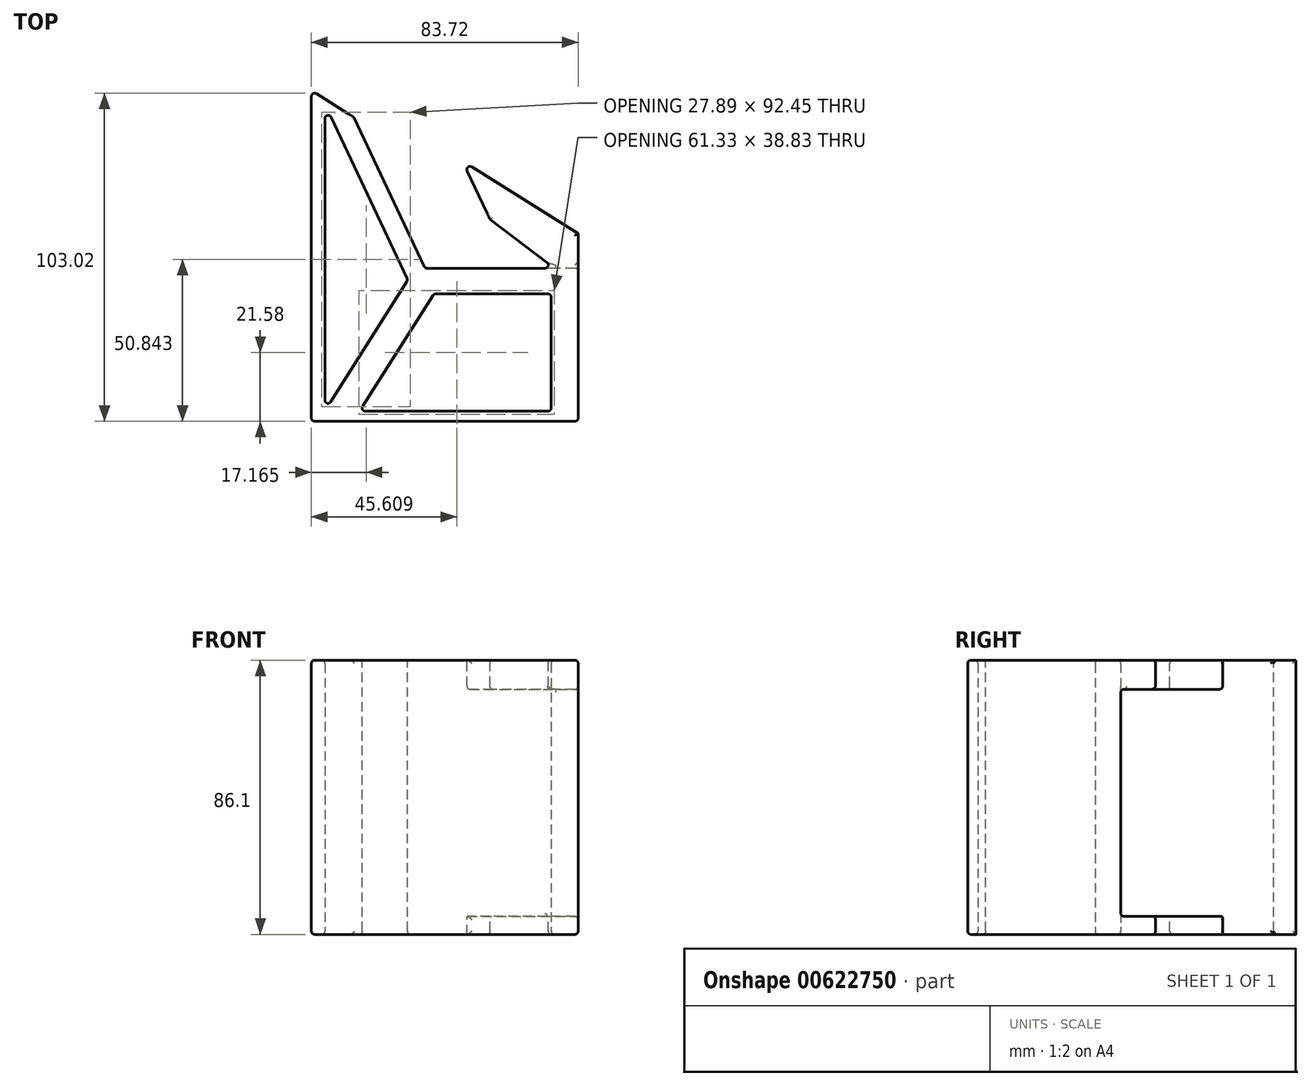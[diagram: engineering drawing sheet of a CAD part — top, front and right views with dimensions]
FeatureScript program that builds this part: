
annotation { "Feature Type Name" : "Feature", "Feature Type Description" : "" }
export const myFeature = defineFeature(function(context is Context, id is Id, definition is map)
    precondition{}
    {
        {
            var Q0;
            Q0=qCreatedBy(makeId("Top.planeOp"),FACE);
            var sketch = newSketch(context, id + "F0", { "sketchPlane" : qUnion([Q0])});
            skLineSegment(sketch, "E0", {"start": v(-40.98, 52.59) * mm, "end": v(-40.98, -58.92) * mm});
            skLineSegment(sketch, "E1", {"start": v(-40.98, -58.92) * mm, "end": v(42.74, -58.92) * mm});
            skLineSegment(sketch, "E2", {"start": v(42.74, -58.92) * mm, "end": v(42.74, 0) * mm});
            skLineSegment(sketch, "E3", {"start": v(42.74, 0) * mm, "end": v(-40.98, 52.59) * mm});
            skLineSegment(sketch, "E4", {"start": v(-36.76, 40.63) * mm, "end": v(-36.76, -55.75) * mm});
            skLineSegment(sketch, "E5", {"start": v(-36.76, -55.75) * mm, "end": v(-10.73, -14.6) * mm});
            skLineSegment(sketch, "E6", {"start": v(-10.73, -14.6) * mm, "end": v(-36.76, 40.63) * mm});
            skLineSegment(sketch, "E7", {"start": v(-25.85, -55.75) * mm, "end": v(-2.56, -18.93) * mm});
            skLineSegment(sketch, "E8", {"start": v(-2.56, -18.93) * mm, "end": v(34.3, -18.93) * mm});
            skLineSegment(sketch, "E9", {"start": v(34.3, -18.93) * mm, "end": v(34.3, -55.75) * mm});
            skLineSegment(sketch, "E10", {"start": v(34.3, -55.75) * mm, "end": v(-25.85, -55.75) * mm});
            skLineSegment(sketch, "E11", {"start": v(-27.8, 36.85) * mm, "end": v(-5.32, -10.86) * mm});
            skLineSegment(sketch, "E12", {"start": v(-5.32, -10.86) * mm, "end": v(35.36, -10.86) * mm});
            skLineSegment(sketch, "E13", {"start": v(35.36, -10.86) * mm, "end": v(-27.8, 36.85) * mm});
            skSolve(sketch);
        }
        {
            var Q0;
            Q0=makeQuery(id+"F0.imprint","IMPRINT",FACE,{"disambiguationData":[TD([[makeQuery(id+"F0.imprint","IMPRINT",EDGE,{"derivedFrom":sQuery(id+"F0.wireOp",EDGE,"E0")}),1.0]])]});
            extrude(context, id + "F1", {"entities" : qUnion([Q0]), "depth" : 86.1 * mm, "offsetDistance" : 25 * mm});
        }
        {
            var Q0;
            Q0=makeQuery(id+"F1.opExtrude","SWEPT_FACE",FACE,{"disambiguationData":[OSD([sQuery(id+"F0.wireOp",EDGE,"E12")])]});
            var sketch = newSketch(context, id + "F2", { "sketchPlane" : qUnion([Q0])});
            skLineSegment(sketch, "E14.bottom", {"start": v(-35.36, 76.97) * mm, "end": v(-6.14, 76.97) * mm});
            skLineSegment(sketch, "E14.top", {"start": v(-35.36, 5.64) * mm, "end": v(-6.14, 5.64) * mm});
            skLineSegment(sketch, "E14.left", {"start": v(-35.36, 76.97) * mm, "end": v(-35.36, 5.64) * mm});
            skLineSegment(sketch, "E14.right", {"start": v(-6.14, 76.97) * mm, "end": v(-6.14, 5.64) * mm});
            skSolve(sketch);
        }
        {
            var Q0;
            Q0=makeQuery(id+"F2.imprint","IMPRINT",FACE,{"disambiguationData":[TD([[makeQuery(id+"F2.imprint","IMPRINT",EDGE,{"derivedFrom":sQuery(id+"F2.wireOp",EDGE,"E14.bottom")}),-1.0]])]});
            var Q1;
            Q1=makeQuery(id+"F1.opExtrude","SWEPT_FACE",FACE,{"disambiguationData":[OSD([sQuery(id+"F0.wireOp",EDGE,"E3")])]});
            extrude(context, id + "F3", {"entities" : qUnion([Q0, Q1]), "operationType" : NewBodyOperationType.REMOVE, "depth" : 74.8 * mm, "offsetDistance" : 25 * mm});
        }
        {
            var Q0;
            Q0=makeQuery(id+"F3.boolean.opBoolean","COPY",FACE,{"derivedFrom":makeQuery(id+"F3.opExtrude","SWEPT_FACE",FACE,{"disambiguationData":[OSD([sQuery(id+"F2.wireOp",EDGE,"E14.left")])]})});
            var sketch = newSketch(context, id + "F4", { "sketchPlane" : qUnion([Q0])});
            skSolve(sketch);
        }
        {
            var Q0;
            {var subQ0=sQuery(id+"F2.wireOp",EDGE,"E14.left");var subQ1=sQuery(id+"F0.wireOp",EDGE,"E13");var subQ2=sQuery(id+"F0.wireOp",EDGE,"E12");Q0=makeQuery(id+"F4.imprint","IMPRINT",FACE,{"disambiguationData":[TD([[makeQuery(id+"F4.imprint","IMPRINT",EDGE,{"derivedFrom":makeQuery(id+"F3.boolean.opBoolean","MERGE",EDGE,{"derivedFrom":[makeQuery(id+"F1.opExtrude","SWEPT_EDGE",EDGE,{"disambiguationData":[OSD([subQ2,subQ1])]}),makeQuery(id+"F3.opExtrude","CAP_EDGE",EDGE,{"disambiguationData":[OSD([subQ0])],"isStart":true})]})}),-1.0]])]});}
            extrude(context, id + "F5", {"entities" : qUnion([Q0]), "operationType" : NewBodyOperationType.REMOVE, "oppositeDirection" : true, "depth" : 25 * mm, "offsetDistance" : 25 * mm});
        }
        {
            var Q0;
            Q0=makeQuery(id+"F1.opExtrude","SWEPT_FACE",FACE,{"disambiguationData":[OSD([sQuery(id+"F0.wireOp",EDGE,"E11")])]});
            extrude(context, id + "F6", {"entities" : qUnion([Q0]), "operationType" : NewBodyOperationType.REMOVE, "depth" : 25 * mm, "offsetDistance" : 25 * mm});
        }
        {
            var Q0;
            {var subQ0=sQuery(id+"F0.wireOp",EDGE,"E0");var subQ11=sQuery(id+"F0.wireOp",EDGE,"E3");Q0=makeQuery(id+"F6.boolean.opBoolean","SPLIT",FACE,{"disambiguationData":[TD([makeQuery(id+"F1.opExtrude","SWEPT_FACE",FACE,{"disambiguationData":[OSD([subQ0])]})])],"derivedFrom":makeQuery(id+"F1.opExtrude","SWEPT_FACE",FACE,{"disambiguationData":[OSD([subQ11])]})});}
            var sketch = newSketch(context, id + "F7", { "sketchPlane" : qUnion([Q0])});
            skLineSegment(sketch, "E15.bottom", {"start": v(62.67, 86.1) * mm, "end": v(39.1, 86.1) * mm});
            skLineSegment(sketch, "E15.top", {"start": v(62.67, 0) * mm, "end": v(39.1, 0) * mm});
            skLineSegment(sketch, "E15.left", {"start": v(62.67, 86.1) * mm, "end": v(62.67, 0) * mm});
            skLineSegment(sketch, "E15.right", {"start": v(39.1, 86.1) * mm, "end": v(39.1, 0) * mm});
            skSolve(sketch);
        }
        {
            var Q0;
            Q0=makeQuery(id+"F7.imprint","IMPRINT",FACE,{"disambiguationData":[TD([[makeQuery(id+"F7.imprint","IMPRINT",EDGE,{"derivedFrom":sQuery(id+"F7.wireOp",EDGE,"E15.bottom")}),-1.0]])]});
            extrude(context, id + "F8", {"entities" : qUnion([Q0]), "operationType" : NewBodyOperationType.REMOVE, "oppositeDirection" : true, "depth" : 6.5 * mm, "offsetDistance" : 25 * mm});
        }
        {
            var Q0;
            Q0=makeQuery(id+"F1.opExtrude","CAP_EDGE",EDGE,{"disambiguationData":[OSD([sQuery(id+"F0.wireOp",EDGE,"E0")])],"isStart":false});
            var Q1;
            Q1=makeQuery(id+"F8.boolean.opBoolean","COPY",EDGE,{"derivedFrom":makeQuery(id+"F8.opExtrude","CAP_EDGE",EDGE,{"disambiguationData":[OSD([sQuery(id+"F7.wireOp",EDGE,"E15.bottom")])],"isStart":false})});
            var Q2;
            Q2=makeQuery(id+"F1.opExtrude","CAP_EDGE",EDGE,{"disambiguationData":[OSD([sQuery(id+"F0.wireOp",EDGE,"E11")])],"isStart":false});
            var Q3;
            Q3=makeQuery(id+"F1.opExtrude","CAP_EDGE",EDGE,{"disambiguationData":[OSD([sQuery(id+"F0.wireOp",EDGE,"E12")])],"isStart":false});
            var Q4;
            Q4=makeQuery(id+"F1.opExtrude","CAP_EDGE",EDGE,{"disambiguationData":[OSD([sQuery(id+"F0.wireOp",EDGE,"E13")])],"isStart":false});
            var Q5;
            {var subQ1=sQuery(id+"F0.wireOp",EDGE,"E3");var subQ2=sQuery(id+"F0.wireOp",EDGE,"E2");Q5=makeQuery(id+"F6.boolean.opBoolean","SPLIT",EDGE,{"disambiguationData":[TD([makeQuery(id+"F1.opExtrude","SWEPT_FACE",FACE,{"disambiguationData":[OSD([subQ2])]})])],"derivedFrom":makeQuery(id+"F1.opExtrude","CAP_EDGE",EDGE,{"disambiguationData":[OSD([subQ1])],"isStart":false})});}
            var Q6;
            {var subQ0=sQuery(id+"F0.wireOp",EDGE,"E11");Q6=makeQuery(id+"F6.boolean.opBoolean","COPY",EDGE,{"derivedFrom":makeQuery(id+"F6.opExtrude","CAP_EDGE",EDGE,{"disambiguationData":[OSD([subQ0]),TDD([makeQuery(id+"F1.opExtrude","CAP_EDGE",EDGE,{"disambiguationData":[OSD([subQ0])],"isStart":false})])],"isStart":false})});}
            var Q7;
            Q7=makeQuery(id+"F1.opExtrude","CAP_EDGE",EDGE,{"disambiguationData":[OSD([sQuery(id+"F0.wireOp",EDGE,"E2")])],"isStart":false});
            var Q8;
            Q8=makeQuery(id+"F1.opExtrude","CAP_EDGE",EDGE,{"disambiguationData":[OSD([sQuery(id+"F0.wireOp",EDGE,"E8")])],"isStart":false});
            var Q9;
            Q9=makeQuery(id+"F1.opExtrude","CAP_EDGE",EDGE,{"disambiguationData":[OSD([sQuery(id+"F0.wireOp",EDGE,"E7")])],"isStart":false});
            var Q10;
            Q10=makeQuery(id+"F1.opExtrude","CAP_EDGE",EDGE,{"disambiguationData":[OSD([sQuery(id+"F0.wireOp",EDGE,"E10")])],"isStart":false});
            var Q11;
            Q11=makeQuery(id+"F1.opExtrude","CAP_EDGE",EDGE,{"disambiguationData":[OSD([sQuery(id+"F0.wireOp",EDGE,"E9")])],"isStart":false});
            var Q12;
            Q12=makeQuery(id+"F1.opExtrude","CAP_EDGE",EDGE,{"disambiguationData":[OSD([sQuery(id+"F0.wireOp",EDGE,"E5")])],"isStart":false});
            var Q13;
            Q13=makeQuery(id+"F1.opExtrude","CAP_EDGE",EDGE,{"disambiguationData":[OSD([sQuery(id+"F0.wireOp",EDGE,"E6")])],"isStart":false});
            var Q14;
            Q14=makeQuery(id+"F1.opExtrude","CAP_EDGE",EDGE,{"disambiguationData":[OSD([sQuery(id+"F0.wireOp",EDGE,"E4")])],"isStart":false});
            var Q15;
            Q15=makeQuery(id+"F1.opExtrude","CAP_EDGE",EDGE,{"disambiguationData":[OSD([sQuery(id+"F0.wireOp",EDGE,"E1")])],"isStart":false});
            var Q16;
            Q16=makeQuery(id+"F5.boolean.opBoolean","INTERSECT",EDGE,{"derivedFrom":[makeQuery(id+"F1.opExtrude","SWEPT_FACE",FACE,{"disambiguationData":[OSD([sQuery(id+"F0.wireOp",EDGE,"E3")])]}),makeQuery(id+"F5.opExtrude","SWEPT_FACE",FACE,{"disambiguationData":[OSD([sQuery(id+"F0.wireOp",EDGE,"E12"),sQuery(id+"F0.wireOp",EDGE,"E13"),sQuery(id+"F2.wireOp",EDGE,"E14.bottom"),sQuery(id+"F2.wireOp",EDGE,"E14.left")])]})]});
            var Q17;
            {var subQ0=sQuery(id+"F2.wireOp",EDGE,"E14.bottom");Q17=makeQuery(id+"F6.boolean.opBoolean","INTERSECT",EDGE,{"derivedFrom":[makeQuery(id+"F5.boolean.opBoolean","MERGE",FACE,{"derivedFrom":[makeQuery(id+"F3.boolean.opBoolean","COPY",FACE,{"derivedFrom":makeQuery(id+"F3.opExtrude","SWEPT_FACE",FACE,{"disambiguationData":[OSD([subQ0])]})}),makeQuery(id+"F5.opExtrude","SWEPT_FACE",FACE,{"disambiguationData":[OSD([sQuery(id+"F0.wireOp",EDGE,"E12"),sQuery(id+"F0.wireOp",EDGE,"E13"),subQ0,sQuery(id+"F2.wireOp",EDGE,"E14.left")])]})]}),makeQuery(id+"F6.opExtrude","CAP_FACE",FACE,{"disambiguationData":[OSD([sQuery(id+"F0.wireOp",EDGE,"E11")])],"isStart":false})]});}
            var Q18;
            Q18=makeQuery(id+"F3.boolean.opBoolean","INTERSECT",EDGE,{"derivedFrom":[makeQuery(id+"F1.opExtrude","SWEPT_FACE",FACE,{"disambiguationData":[OSD([sQuery(id+"F0.wireOp",EDGE,"E13")])]}),makeQuery(id+"F3.opExtrude","SWEPT_FACE",FACE,{"disambiguationData":[OSD([sQuery(id+"F2.wireOp",EDGE,"E14.bottom")])]})]});
            var Q19;
            Q19=makeQuery(id+"F5.boolean.opBoolean","INTERSECT",EDGE,{"derivedFrom":[makeQuery(id+"F1.opExtrude","SWEPT_FACE",FACE,{"disambiguationData":[OSD([sQuery(id+"F0.wireOp",EDGE,"E2")])]}),makeQuery(id+"F5.opExtrude","SWEPT_FACE",FACE,{"disambiguationData":[OSD([sQuery(id+"F0.wireOp",EDGE,"E12"),sQuery(id+"F0.wireOp",EDGE,"E13"),sQuery(id+"F2.wireOp",EDGE,"E14.left")])]})]});
            var Q20;
            Q20=makeQuery(id+"F5.boolean.opBoolean","INTERSECT",EDGE,{"derivedFrom":[makeQuery(id+"F1.opExtrude","SWEPT_FACE",FACE,{"disambiguationData":[OSD([sQuery(id+"F0.wireOp",EDGE,"E2")])]}),makeQuery(id+"F5.opExtrude","SWEPT_FACE",FACE,{"disambiguationData":[OSD([sQuery(id+"F0.wireOp",EDGE,"E12"),sQuery(id+"F0.wireOp",EDGE,"E13"),sQuery(id+"F2.wireOp",EDGE,"E14.top"),sQuery(id+"F2.wireOp",EDGE,"E14.left")])]})]});
            var Q21;
            Q21=makeQuery(id+"F5.boolean.opBoolean","INTERSECT",EDGE,{"derivedFrom":[makeQuery(id+"F1.opExtrude","SWEPT_FACE",FACE,{"disambiguationData":[OSD([sQuery(id+"F0.wireOp",EDGE,"E3")])]}),makeQuery(id+"F5.opExtrude","SWEPT_FACE",FACE,{"disambiguationData":[OSD([sQuery(id+"F0.wireOp",EDGE,"E12"),sQuery(id+"F0.wireOp",EDGE,"E13"),sQuery(id+"F2.wireOp",EDGE,"E14.top"),sQuery(id+"F2.wireOp",EDGE,"E14.left")])]})]});
            var Q22;
            {var subQ1=sQuery(id+"F0.wireOp",EDGE,"E3");var subQ2=sQuery(id+"F0.wireOp",EDGE,"E2");Q22=makeQuery(id+"F6.boolean.opBoolean","SPLIT",EDGE,{"disambiguationData":[TD([makeQuery(id+"F1.opExtrude","SWEPT_FACE",FACE,{"disambiguationData":[OSD([subQ2])]})])],"derivedFrom":makeQuery(id+"F1.opExtrude","CAP_EDGE",EDGE,{"disambiguationData":[OSD([subQ1])],"isStart":true})});}
            var Q23;
            {var subQ0=sQuery(id+"F0.wireOp",EDGE,"E11");Q23=makeQuery(id+"F6.boolean.opBoolean","COPY",EDGE,{"derivedFrom":makeQuery(id+"F6.opExtrude","CAP_EDGE",EDGE,{"disambiguationData":[OSD([subQ0]),TDD([makeQuery(id+"F1.opExtrude","CAP_EDGE",EDGE,{"disambiguationData":[OSD([subQ0])],"isStart":true})])],"isStart":false})});}
            var Q24;
            Q24=makeQuery(id+"F1.opExtrude","CAP_EDGE",EDGE,{"disambiguationData":[OSD([sQuery(id+"F0.wireOp",EDGE,"E13")])],"isStart":true});
            var Q25;
            Q25=makeQuery(id+"F1.opExtrude","CAP_EDGE",EDGE,{"disambiguationData":[OSD([sQuery(id+"F0.wireOp",EDGE,"E2")])],"isStart":true});
            var Q26;
            Q26=makeQuery(id+"F1.opExtrude","CAP_EDGE",EDGE,{"disambiguationData":[OSD([sQuery(id+"F0.wireOp",EDGE,"E12")])],"isStart":true});
            var Q27;
            Q27=makeQuery(id+"F1.opExtrude","CAP_EDGE",EDGE,{"disambiguationData":[OSD([sQuery(id+"F0.wireOp",EDGE,"E9")])],"isStart":true});
            var Q28;
            Q28=makeQuery(id+"F1.opExtrude","CAP_EDGE",EDGE,{"disambiguationData":[OSD([sQuery(id+"F0.wireOp",EDGE,"E8")])],"isStart":true});
            var Q29;
            Q29=makeQuery(id+"F1.opExtrude","CAP_EDGE",EDGE,{"disambiguationData":[OSD([sQuery(id+"F0.wireOp",EDGE,"E7")])],"isStart":true});
            var Q30;
            Q30=makeQuery(id+"F1.opExtrude","CAP_EDGE",EDGE,{"disambiguationData":[OSD([sQuery(id+"F0.wireOp",EDGE,"E10")])],"isStart":true});
            var Q31;
            Q31=makeQuery(id+"F1.opExtrude","CAP_EDGE",EDGE,{"disambiguationData":[OSD([sQuery(id+"F0.wireOp",EDGE,"E1")])],"isStart":true});
            var Q32;
            Q32=makeQuery(id+"F1.opExtrude","SWEPT_EDGE",EDGE,{"disambiguationData":[OSD([sQuery(id+"F0.wireOp",EDGE,"E1"),sQuery(id+"F0.wireOp",EDGE,"E2")])]});
            var Q33;
            Q33=makeQuery(id+"F1.opExtrude","SWEPT_FACE",FACE,{"disambiguationData":[OSD([sQuery(id+"F0.wireOp",EDGE,"E7")])]});
            var Q34;
            Q34=makeQuery(id+"F8.boolean.opBoolean","INTERSECT",EDGE,{"derivedFrom":[makeQuery(id+"F1.opExtrude","SWEPT_FACE",FACE,{"disambiguationData":[OSD([sQuery(id+"F0.wireOp",EDGE,"E11")])]}),makeQuery(id+"F8.opExtrude","CAP_FACE",FACE,{"disambiguationData":[OSD([sQuery(id+"F7.wireOp",EDGE,"E15.bottom"),sQuery(id+"F7.wireOp",EDGE,"E15.top"),sQuery(id+"F7.wireOp",EDGE,"E15.left"),sQuery(id+"F7.wireOp",EDGE,"E15.right")])],"isStart":false})]});
            var Q35;
            Q35=makeQuery(id+"F8.boolean.opBoolean","INTERSECT",EDGE,{"derivedFrom":[makeQuery(id+"F1.opExtrude","SWEPT_FACE",FACE,{"disambiguationData":[OSD([sQuery(id+"F0.wireOp",EDGE,"E0")])]}),makeQuery(id+"F8.opExtrude","CAP_FACE",FACE,{"disambiguationData":[OSD([sQuery(id+"F7.wireOp",EDGE,"E15.bottom"),sQuery(id+"F7.wireOp",EDGE,"E15.top"),sQuery(id+"F7.wireOp",EDGE,"E15.left"),sQuery(id+"F7.wireOp",EDGE,"E15.right")])],"isStart":false})]});
            var Q36;
            Q36=makeQuery(id+"F8.boolean.opBoolean","COPY",EDGE,{"derivedFrom":makeQuery(id+"F8.opExtrude","CAP_EDGE",EDGE,{"disambiguationData":[OSD([sQuery(id+"F7.wireOp",EDGE,"E15.top")])],"isStart":false})});
            var Q37;
            Q37=makeQuery(id+"F1.opExtrude","CAP_EDGE",EDGE,{"disambiguationData":[OSD([sQuery(id+"F0.wireOp",EDGE,"E11")])],"isStart":true});
            var Q38;
            Q38=makeQuery(id+"F1.opExtrude","CAP_EDGE",EDGE,{"disambiguationData":[OSD([sQuery(id+"F0.wireOp",EDGE,"E6")])],"isStart":true});
            var Q39;
            Q39=makeQuery(id+"F1.opExtrude","CAP_EDGE",EDGE,{"disambiguationData":[OSD([sQuery(id+"F0.wireOp",EDGE,"E4")])],"isStart":true});
            var Q40;
            Q40=makeQuery(id+"F1.opExtrude","CAP_EDGE",EDGE,{"disambiguationData":[OSD([sQuery(id+"F0.wireOp",EDGE,"E5")])],"isStart":true});
            var Q41;
            Q41=makeQuery(id+"F1.opExtrude","CAP_EDGE",EDGE,{"disambiguationData":[OSD([sQuery(id+"F0.wireOp",EDGE,"E0")])],"isStart":true});
            var Q42;
            Q42=makeQuery(id+"F6.boolean.opBoolean","INTERSECT",EDGE,{"disambiguationData":[OD(1.0)],"derivedFrom":[makeQuery(id+"F1.opExtrude","SWEPT_FACE",FACE,{"disambiguationData":[OSD([sQuery(id+"F0.wireOp",EDGE,"E3")])]}),makeQuery(id+"F6.opExtrude","CAP_FACE",FACE,{"disambiguationData":[OSD([sQuery(id+"F0.wireOp",EDGE,"E11")])],"isStart":false})]});
            var Q43;
            Q43=makeQuery(id+"F6.boolean.opBoolean","INTERSECT",EDGE,{"disambiguationData":[OD(0.0)],"derivedFrom":[makeQuery(id+"F1.opExtrude","SWEPT_FACE",FACE,{"disambiguationData":[OSD([sQuery(id+"F0.wireOp",EDGE,"E3")])]}),makeQuery(id+"F6.opExtrude","CAP_FACE",FACE,{"disambiguationData":[OSD([sQuery(id+"F0.wireOp",EDGE,"E11")])],"isStart":false})]});
            var Q44;
            Q44=makeQuery(id+"F1.opExtrude","SWEPT_EDGE",EDGE,{"disambiguationData":[OSD([sQuery(id+"F0.wireOp",EDGE,"E11"),sQuery(id+"F0.wireOp",EDGE,"E12")])]});
            var Q45;
            {var subQ0=sQuery(id+"F0.wireOp",EDGE,"E12");Q45=makeQuery(id+"F5.boolean.opBoolean","MERGE",FACE,{"derivedFrom":[makeQuery(id+"F1.opExtrude","SWEPT_FACE",FACE,{"disambiguationData":[OSD([subQ0])]}),makeQuery(id+"F5.opExtrude","SWEPT_FACE",FACE,{"disambiguationData":[OSD([subQ0,sQuery(id+"F0.wireOp",EDGE,"E13"),sQuery(id+"F2.wireOp",EDGE,"E14.left")])]})]});}
            var Q46;
            Q46=makeQuery(id+"F1.opExtrude","SWEPT_FACE",FACE,{"disambiguationData":[OSD([sQuery(id+"F0.wireOp",EDGE,"E11")])]});
            var Q47;
            Q47=makeQuery(id+"F1.opExtrude","SWEPT_FACE",FACE,{"disambiguationData":[OSD([sQuery(id+"F0.wireOp",EDGE,"E1")])]});
            var Q48;
            Q48=makeQuery(id+"F1.opExtrude","SWEPT_EDGE",EDGE,{"disambiguationData":[OSD([sQuery(id+"F0.wireOp",EDGE,"E5"),sQuery(id+"F0.wireOp",EDGE,"E6")])]});
            var Q49;
            Q49=makeQuery(id+"F1.opExtrude","SWEPT_EDGE",EDGE,{"disambiguationData":[OSD([sQuery(id+"F0.wireOp",EDGE,"E7"),sQuery(id+"F0.wireOp",EDGE,"E10")])]});
            var Q50;
            Q50=makeQuery(id+"F1.opExtrude","SWEPT_EDGE",EDGE,{"disambiguationData":[OSD([sQuery(id+"F0.wireOp",EDGE,"E7"),sQuery(id+"F0.wireOp",EDGE,"E8")])]});
            var Q51;
            Q51=makeQuery(id+"F1.opExtrude","SWEPT_FACE",FACE,{"disambiguationData":[OSD([sQuery(id+"F0.wireOp",EDGE,"E6")])]});
            var Q52;
            Q52=makeQuery(id+"F1.opExtrude","SWEPT_FACE",FACE,{"disambiguationData":[OSD([sQuery(id+"F0.wireOp",EDGE,"E8")])]});
            var Q53;
            Q53=makeQuery(id+"F1.opExtrude","SWEPT_FACE",FACE,{"disambiguationData":[OSD([sQuery(id+"F0.wireOp",EDGE,"E10")])]});
            var Q54;
            Q54=makeQuery(id+"F1.opExtrude","SWEPT_EDGE",EDGE,{"disambiguationData":[OSD([sQuery(id+"F0.wireOp",EDGE,"E4"),sQuery(id+"F0.wireOp",EDGE,"E5")])]});
            var Q55;
            Q55=makeQuery(id+"F1.opExtrude","SWEPT_FACE",FACE,{"disambiguationData":[OSD([sQuery(id+"F0.wireOp",EDGE,"E4")])]});
            var Q56;
            Q56=makeQuery(id+"F1.opExtrude","SWEPT_FACE",FACE,{"disambiguationData":[OSD([sQuery(id+"F0.wireOp",EDGE,"E5")])]});
            var Q57;
            Q57=makeQuery(id+"F1.opExtrude","SWEPT_EDGE",EDGE,{"disambiguationData":[OSD([sQuery(id+"F0.wireOp",EDGE,"E0"),sQuery(id+"F0.wireOp",EDGE,"E1")])]});
            var Q58;
            Q58=makeQuery(id+"F1.opExtrude","SWEPT_FACE",FACE,{"disambiguationData":[OSD([sQuery(id+"F0.wireOp",EDGE,"E0")])]});
            fillet(context, id + "F9", {"entities" : qUnion([Q0, Q1, Q2, Q3, Q4, Q5, Q6, Q7, Q8, Q9, Q10, Q11, Q12, Q13, Q14, Q15, Q16, Q17, Q18, Q19, Q20, Q21, Q22, Q23, Q24, Q25, Q26, Q27, Q28, Q29, Q30, Q31, Q32, Q33, Q34, Q35, Q36, Q37, Q38, Q39, Q40, Q41, Q42, Q43, Q44, Q45, Q46, Q47, Q48, Q49, Q50, Q51, Q52, Q53, Q54, Q55, Q56, Q57, Q58]), "radius" : 1 * mm, "tangentPropagation" : true, "allowEdgeOverflow" : false});
        }
    });
